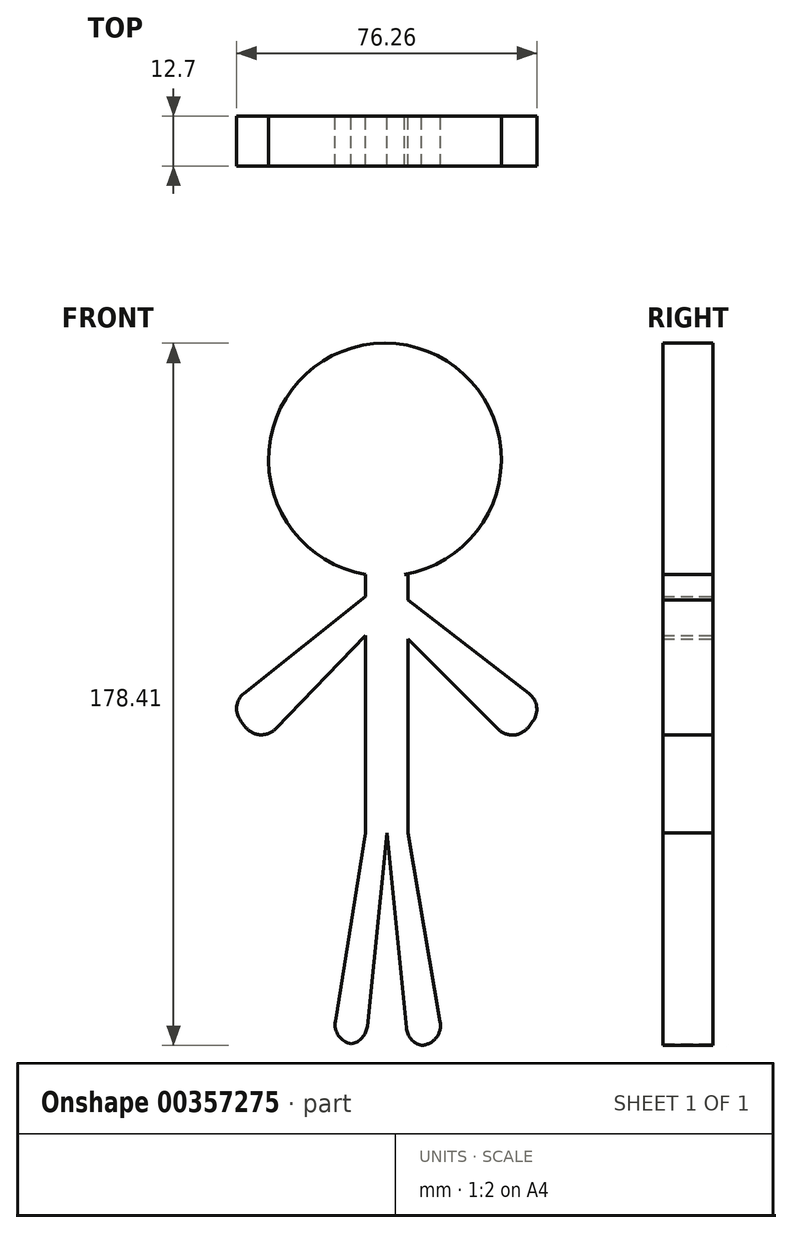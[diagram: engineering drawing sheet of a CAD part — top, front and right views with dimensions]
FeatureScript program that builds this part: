
annotation { "Feature Type Name" : "Feature", "Feature Type Description" : "" }
export const myFeature = defineFeature(function(context is Context, id is Id, definition is map)
    precondition{}
    {
        {
            var Q0;
            Q0=qCreatedBy(makeId("Front.planeOp"),FACE);
            var sketch = newSketch(context, id + "F0", { "sketchPlane" : qUnion([Q0])});
            skCircle(sketch, "E0", {"center": v(0, 62.53) * mm, "radius": 29.58 * mm});
            skLineSegment(sketch, "E1.bottom", {"start": v(-4.94, 33.37) * mm, "end": v(5.87, 33.37) * mm});
            skLineSegment(sketch, "E1.top", {"start": v(-4.94, -32.28) * mm, "end": v(5.87, -32.28) * mm});
            skLineSegment(sketch, "E1.left", {"start": v(-4.94, 33.37) * mm, "end": v(-4.94, -32.28) * mm});
            skLineSegment(sketch, "E1.right", {"start": v(5.87, 33.37) * mm, "end": v(5.87, -32.28) * mm});
            skLineSegment(sketch, "E2", {"start": v(-4.94, -32.28) * mm, "end": v(-13.55, -86.01) * mm});
            skLineSegment(sketch, "E3", {"start": v(-13.55, -86.01) * mm, "end": v(-4.94, -86.01) * mm});
            skLineSegment(sketch, "E4", {"start": v(-4.94, -86.01) * mm, "end": v(0.46, -32.28) * mm});
            skLineSegment(sketch, "E5", {"start": v(0.46, -32.28) * mm, "end": v(5.87, -86.01) * mm});
            skLineSegment(sketch, "E6", {"start": v(5.87, -86.01) * mm, "end": v(15.17, -86.95) * mm});
            skLineSegment(sketch, "E7", {"start": v(15.17, -86.95) * mm, "end": v(5.87, -32.28) * mm});
            skLineSegment(sketch, "E8", {"start": v(-4.94, 27.77) * mm, "end": v(-39.73, 0) * mm});
            skLineSegment(sketch, "E9", {"start": v(-39.73, 0) * mm, "end": v(-31.75, -10) * mm});
            skLineSegment(sketch, "E10", {"start": v(-31.75, -10) * mm, "end": v(-4.94, 17.83) * mm});
            skLineSegment(sketch, "E11", {"start": v(5.87, 26.86) * mm, "end": v(40.64, 0) * mm});
            skLineSegment(sketch, "E12", {"start": v(40.64, 0) * mm, "end": v(32.88, -10.04) * mm});
            skLineSegment(sketch, "E13", {"start": v(32.88, -10.04) * mm, "end": v(5.87, 16.93) * mm});
            skSolve(sketch);
        }
        {
            var Q0;
            Q0 = qSketchRegion(id + "F0", true);
            extrude(context, id + "F1", {"entities" : qUnion([Q0]), "depth" : 12.7 * mm});
        }
        {
            var Q0;
            Q0=makeQuery(id+"F1.opExtrude","SWEPT_EDGE",EDGE,{"disambiguationData":[OSD([sQuery(id+"F0.wireOp",EDGE,"E11"),sQuery(id+"F0.wireOp",EDGE,"E12")])]});
            var Q1;
            Q1=makeQuery(id+"F1.opExtrude","SWEPT_EDGE",EDGE,{"disambiguationData":[OSD([sQuery(id+"F0.wireOp",EDGE,"E9"),sQuery(id+"F0.wireOp",EDGE,"E10")])]});
            var Q2;
            Q2=makeQuery(id+"F1.opExtrude","SWEPT_EDGE",EDGE,{"disambiguationData":[OSD([sQuery(id+"F0.wireOp",EDGE,"E12"),sQuery(id+"F0.wireOp",EDGE,"E13")])]});
            var Q3;
            Q3=makeQuery(id+"F1.opExtrude","SWEPT_EDGE",EDGE,{"disambiguationData":[OSD([sQuery(id+"F0.wireOp",EDGE,"E8"),sQuery(id+"F0.wireOp",EDGE,"E9")])]});
            var Q4;
            Q4=makeQuery(id+"F1.opExtrude","SWEPT_EDGE",EDGE,{"disambiguationData":[OSD([sQuery(id+"F0.wireOp",EDGE,"E3"),sQuery(id+"F0.wireOp",EDGE,"E4")])]});
            var Q5;
            Q5=makeQuery(id+"F1.opExtrude","SWEPT_EDGE",EDGE,{"disambiguationData":[OSD([sQuery(id+"F0.wireOp",EDGE,"E5"),sQuery(id+"F0.wireOp",EDGE,"E6")])]});
            var Q6;
            Q6=makeQuery(id+"F1.opExtrude","SWEPT_EDGE",EDGE,{"disambiguationData":[OSD([sQuery(id+"F0.wireOp",EDGE,"E2"),sQuery(id+"F0.wireOp",EDGE,"E3")])]});
            var Q7;
            Q7=makeQuery(id+"F1.opExtrude","SWEPT_EDGE",EDGE,{"disambiguationData":[OSD([sQuery(id+"F0.wireOp",EDGE,"E6"),sQuery(id+"F0.wireOp",EDGE,"E7")])]});
            fillet(context, id + "F2", {"entities" : qUnion([Q0, Q1, Q2, Q3, Q4, Q5, Q6, Q7]), "radius" : 5.08 * mm, "tangentPropagation" : true, "allowEdgeOverflow" : false});
        }
    });
